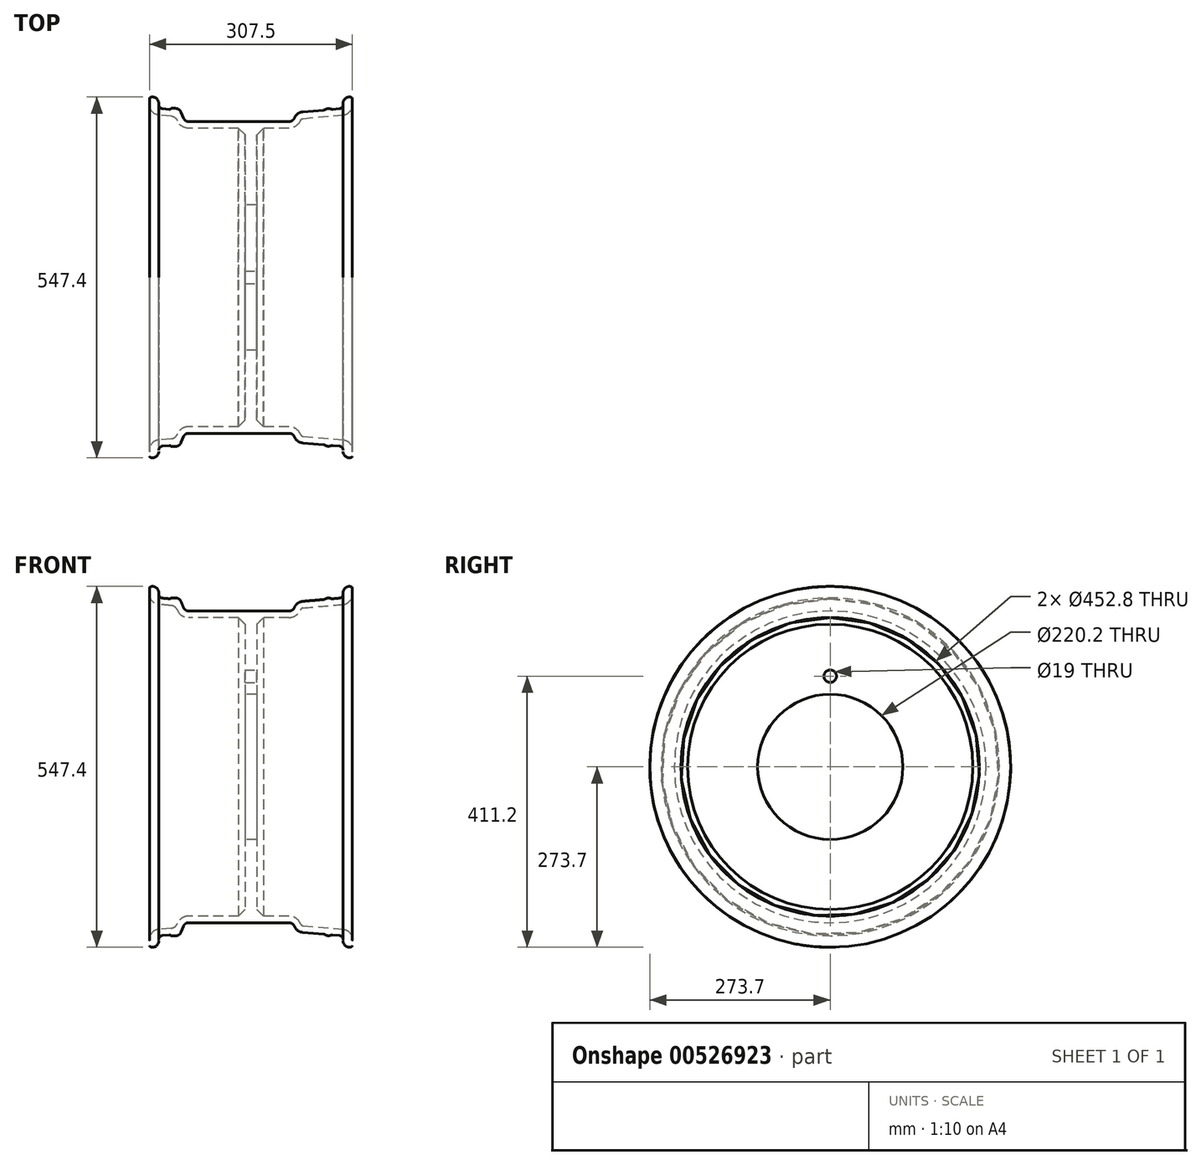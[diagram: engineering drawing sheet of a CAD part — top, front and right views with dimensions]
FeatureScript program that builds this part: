
annotation { "Feature Type Name" : "Feature", "Feature Type Description" : "" }
export const myFeature = defineFeature(function(context is Context, id is Id, definition is map)
    precondition{}
    {
        {
            var Q0;
            Q0=qCreatedBy(makeId("Top.planeOp"),FACE);
            var sketch = newSketch(context, id + "F0", { "sketchPlane" : qUnion([Q0])});
            skArc(sketch, "E0", {"start": v(-69.83, 132) * mm, "mid": v(-71.25, 135.43) * mm, "end": v(-74.68, 136.85) * mm});
            skArc(sketch, "E1", {"start": v(-74.68, 136.85) * mm, "mid": v(-75.64, 136.7) * mm, "end": v(-76.5, 136.28) * mm});
            skArc(sketch, "E2", {"start": v(-76.5, 136.28) * mm, "mid": v(-76.74, 136) * mm, "end": v(-76.83, 135.66) * mm});
            skArc(sketch, "E3", {"start": v(-76.83, 130.67) * mm, "mid": v(-74.86, 125.6) * mm, "end": v(-69.98, 123.2) * mm});
            skLineSegment(sketch, "E4", {"start": v(-69.98, 123.2) * mm, "end": v(-60.45, 122.36) * mm});
            skArc(sketch, "E5", {"start": v(-55.67, 118.83) * mm, "mid": v(-57.56, 121.27) * mm, "end": v(-60.45, 122.36) * mm});
            skArc(sketch, "E6", {"start": v(-55.67, 118.83) * mm, "mid": v(-52.36, 114.74) * mm, "end": v(-47.33, 113.2) * mm});
            skLineSegment(sketch, "E7", {"start": v(-51.04, 120.7) * mm, "end": v(-52.84, 125.17) * mm});
            skArc(sketch, "E8", {"start": v(-52.84, 125.17) * mm, "mid": v(-54.63, 127.37) * mm, "end": v(-57.34, 128.2) * mm});
            skLineSegment(sketch, "E9", {"start": v(-60.08, 128.2) * mm, "end": v(-57.34, 128.2) * mm});
            skArc(sketch, "E10", {"start": v(-60.08, 128.2) * mm, "mid": v(-60.37, 128.14) * mm, "end": v(-60.62, 127.97) * mm});
            skArc(sketch, "E11", {"start": v(-61.84, 127.5) * mm, "mid": v(-61.18, 127.6) * mm, "end": v(-60.62, 127.97) * mm});
            skLineSegment(sketch, "E12", {"start": v(-67.09, 127.96) * mm, "end": v(-61.84, 127.5) * mm});
            skArc(sketch, "E13", {"start": v(-69.83, 130.95) * mm, "mid": v(-69.04, 128.92) * mm, "end": v(-67.09, 127.96) * mm});
            skArc(sketch, "E14", {"start": v(67.18, 127.96) * mm, "mid": v(69.13, 128.92) * mm, "end": v(69.92, 130.95) * mm});
            skLineSegment(sketch, "E15", {"start": v(62.04, 127.51) * mm, "end": v(67.18, 127.96) * mm});
            skArc(sketch, "E16", {"start": v(60.67, 127.71) * mm, "mid": v(61.34, 127.53) * mm, "end": v(62.04, 127.51) * mm});
            skArc(sketch, "E17", {"start": v(60.67, 127.71) * mm, "mid": v(58.51, 128.03) * mm, "end": v(56.45, 127.35) * mm});
            skArc(sketch, "E18", {"start": v(55.13, 126.9) * mm, "mid": v(55.81, 127.05) * mm, "end": v(56.45, 127.35) * mm});
            skLineSegment(sketch, "E19", {"start": v(39.33, 125.52) * mm, "end": v(55.13, 126.9) * mm});
            skArc(sketch, "E20", {"start": v(39.33, 125.52) * mm, "mid": v(35.57, 124.11) * mm, "end": v(33.07, 120.96) * mm});
            skArc(sketch, "E21", {"start": v(28.92, 118.2) * mm, "mid": v(31.41, 118.95) * mm, "end": v(33.07, 120.96) * mm});
            skLineSegment(sketch, "E22", {"start": v(-47.33, 113.2) * mm, "end": v(28.86, 113.2) * mm});
            skArc(sketch, "E23", {"start": v(28.86, 113.2) * mm, "mid": v(34.12, 114.79) * mm, "end": v(37.62, 119.02) * mm});
            skArc(sketch, "E24", {"start": v(39.7, 120.54) * mm, "mid": v(38.45, 120.07) * mm, "end": v(37.62, 119.02) * mm});
            skLineSegment(sketch, "E25", {"start": v(70.08, 123.2) * mm, "end": v(39.7, 120.54) * mm});
            skArc(sketch, "E26", {"start": v(70.08, 123.2) * mm, "mid": v(74.95, 125.6) * mm, "end": v(76.92, 130.67) * mm});
            skArc(sketch, "E27", {"start": v(76.92, 135.66) * mm, "mid": v(76.84, 136) * mm, "end": v(76.6, 136.28) * mm});
            skArc(sketch, "E28", {"start": v(76.6, 136.28) * mm, "mid": v(75.73, 136.7) * mm, "end": v(74.77, 136.85) * mm});
            skArc(sketch, "E29", {"start": v(74.77, 136.85) * mm, "mid": v(71.34, 135.43) * mm, "end": v(69.92, 132) * mm});
            skLineSegment(sketch, "E30", {"start": v(-47.33, 118.2) * mm, "end": v(28.92, 118.2) * mm});
            skArc(sketch, "E31", {"start": v(-51.04, 120.7) * mm, "mid": v(-49.57, 118.88) * mm, "end": v(-47.33, 118.2) * mm});
            skLineSegment(sketch, "E32", {"start": v(76.92, 135.66) * mm, "end": v(76.92, 130.67) * mm});
            skLineSegment(sketch, "E33", {"start": v(69.92, 130.95) * mm, "end": v(69.92, 132) * mm});
            skLineSegment(sketch, "E34", {"start": v(-76.83, 130.67) * mm, "end": v(-76.83, 135.66) * mm});
            skLineSegment(sketch, "E35", {"start": v(-69.83, 132) * mm, "end": v(-69.83, 130.95) * mm});
            skLineSegment(sketch, "E36", {"start": v(-4.5, 108.25) * mm, "end": v(-9.45, 113.2) * mm});
            skLineSegment(sketch, "E37", {"start": v(4.5, 108.15) * mm, "end": v(9.55, 113.2) * mm});
            skLineSegment(sketch, "E38", {"start": v(-4.5, 113.2) * mm, "end": v(-4.5, 55.05) * mm});
            skLineSegment(sketch, "E39", {"start": v(4.5, 113.2) * mm, "end": v(4.5, 55.05) * mm});
            skLineSegment(sketch, "E40", {"start": v(-4.5, 55.05) * mm, "end": v(4.5, 55.05) * mm});
            skLineSegment(sketch, "E41", {"start": v(-54.5, 0) * mm, "end": v(54.5, 0) * mm, "construction": true});
            skSolve(sketch);
        }
        {
            var Q0;
            Q0 = qSketchRegion(id + "F0", true);
            var Q1;
            Q1=sQuery(id+"F0.wireOp",EDGE,"E41");
            revolve(context, id + "F1", {"entities" : qUnion([Q0]), "axis" : qUnion([Q1]), "revolveType" : RevolveType.FULL});
        }
        {
            var Q0;
            Q0=makeQuery(id+"F1.opRevolve","SWEPT_BODY",BODY,{"disambiguationData":[OSD([sQuery(id+"F0.wireOp",EDGE,"E0"),sQuery(id+"F0.wireOp",EDGE,"E1"),sQuery(id+"F0.wireOp",EDGE,"E2"),sQuery(id+"F0.wireOp",EDGE,"E3"),sQuery(id+"F0.wireOp",EDGE,"E4"),sQuery(id+"F0.wireOp",EDGE,"E5"),sQuery(id+"F0.wireOp",EDGE,"E6"),sQuery(id+"F0.wireOp",EDGE,"E7"),sQuery(id+"F0.wireOp",EDGE,"E8"),sQuery(id+"F0.wireOp",EDGE,"E9"),sQuery(id+"F0.wireOp",EDGE,"E10"),sQuery(id+"F0.wireOp",EDGE,"E11"),sQuery(id+"F0.wireOp",EDGE,"E12"),sQuery(id+"F0.wireOp",EDGE,"E13"),sQuery(id+"F0.wireOp",EDGE,"E14"),sQuery(id+"F0.wireOp",EDGE,"E15"),sQuery(id+"F0.wireOp",EDGE,"E16"),sQuery(id+"F0.wireOp",EDGE,"E17"),sQuery(id+"F0.wireOp",EDGE,"E18"),sQuery(id+"F0.wireOp",EDGE,"E19"),sQuery(id+"F0.wireOp",EDGE,"E20"),sQuery(id+"F0.wireOp",EDGE,"E21"),sQuery(id+"F0.wireOp",EDGE,"E22"),sQuery(id+"F0.wireOp",EDGE,"E23"),sQuery(id+"F0.wireOp",EDGE,"E24"),sQuery(id+"F0.wireOp",EDGE,"E25"),sQuery(id+"F0.wireOp",EDGE,"E26"),sQuery(id+"F0.wireOp",EDGE,"E27"),sQuery(id+"F0.wireOp",EDGE,"E28"),sQuery(id+"F0.wireOp",EDGE,"E29"),sQuery(id+"F0.wireOp",EDGE,"E30"),sQuery(id+"F0.wireOp",EDGE,"E31"),sQuery(id+"F0.wireOp",EDGE,"E32"),sQuery(id+"F0.wireOp",EDGE,"E33"),sQuery(id+"F0.wireOp",EDGE,"E34"),sQuery(id+"F0.wireOp",EDGE,"E35"),sQuery(id+"F0.wireOp",EDGE,"E36"),sQuery(id+"F0.wireOp",EDGE,"E37"),sQuery(id+"F0.wireOp",EDGE,"E38"),sQuery(id+"F0.wireOp",EDGE,"E39"),sQuery(id+"F0.wireOp",EDGE,"E40")])]});
            var Q1;
            Q1=qCreatedBy(makeId("Origin.pointOp"),VERTEX);
            transform(context, id + "F2", {"entities" : qUnion([Q0]), "transformType" : TransformType.SCALE_UNIFORMLY, "scale" : 2, "scalePoint" : qUnion([Q1]), "makeCopy" : false});
        }
        {
            var Q0;
            Q0=makeQuery(id+"F1.opRevolve","SWEPT_FACE",FACE,{"disambiguationData":[OSD([sQuery(id+"F0.wireOp",EDGE,"E39")])]});
            var sketch = newSketch(context, id + "F3", { "sketchPlane" : qUnion([Q0])});
            skCircle(sketch, "E42", {"center": v(0, 0) * mm, "radius": 137.5 * mm, "construction": true});
            skLineSegment(sketch, "E43", {"start": v(0, 0) * mm, "end": v(0, 137.5) * mm, "construction": true});
            skPoint(sketch, "E44", {"position": v(0, 137.5) * mm});
            skSolve(sketch);
        }
        {
            var Q0;
            Q0=sQuery(id+"F3.wireOp",VERTEX,"E44");
            var Q1;
            Q1=makeQuery(id+"F1.opRevolve","SWEPT_BODY",BODY,{"disambiguationData":[OSD([sQuery(id+"F0.wireOp",EDGE,"E0"),sQuery(id+"F0.wireOp",EDGE,"E1"),sQuery(id+"F0.wireOp",EDGE,"E2"),sQuery(id+"F0.wireOp",EDGE,"E3"),sQuery(id+"F0.wireOp",EDGE,"E4"),sQuery(id+"F0.wireOp",EDGE,"E5"),sQuery(id+"F0.wireOp",EDGE,"E6"),sQuery(id+"F0.wireOp",EDGE,"E7"),sQuery(id+"F0.wireOp",EDGE,"E8"),sQuery(id+"F0.wireOp",EDGE,"E9"),sQuery(id+"F0.wireOp",EDGE,"E10"),sQuery(id+"F0.wireOp",EDGE,"E11"),sQuery(id+"F0.wireOp",EDGE,"E12"),sQuery(id+"F0.wireOp",EDGE,"E13"),sQuery(id+"F0.wireOp",EDGE,"E14"),sQuery(id+"F0.wireOp",EDGE,"E15"),sQuery(id+"F0.wireOp",EDGE,"E16"),sQuery(id+"F0.wireOp",EDGE,"E17"),sQuery(id+"F0.wireOp",EDGE,"E18"),sQuery(id+"F0.wireOp",EDGE,"E19"),sQuery(id+"F0.wireOp",EDGE,"E20"),sQuery(id+"F0.wireOp",EDGE,"E21"),sQuery(id+"F0.wireOp",EDGE,"E22"),sQuery(id+"F0.wireOp",EDGE,"E23"),sQuery(id+"F0.wireOp",EDGE,"E24"),sQuery(id+"F0.wireOp",EDGE,"E25"),sQuery(id+"F0.wireOp",EDGE,"E26"),sQuery(id+"F0.wireOp",EDGE,"E27"),sQuery(id+"F0.wireOp",EDGE,"E28"),sQuery(id+"F0.wireOp",EDGE,"E29"),sQuery(id+"F0.wireOp",EDGE,"E30"),sQuery(id+"F0.wireOp",EDGE,"E31"),sQuery(id+"F0.wireOp",EDGE,"E32"),sQuery(id+"F0.wireOp",EDGE,"E33"),sQuery(id+"F0.wireOp",EDGE,"E34"),sQuery(id+"F0.wireOp",EDGE,"E35"),sQuery(id+"F0.wireOp",EDGE,"E36"),sQuery(id+"F0.wireOp",EDGE,"E37"),sQuery(id+"F0.wireOp",EDGE,"E38"),sQuery(id+"F0.wireOp",EDGE,"E39"),sQuery(id+"F0.wireOp",EDGE,"E40")])]});
            hole(context, id + "F4", {"style" : HoleStyle.SIMPLE, "endStyle" : HoleEndStyle.THROUGH, "holeDiameter" : 19 * mm, "majorDiameter" : 5 * mm, "isTappedThrough" : true, "tappedDepth" : 12 * mm, "tapClearance" : 3, "startFromSketch" : true, "locations" : qUnion([Q0]), "scope" : qUnion([Q1])});
        }
    });
